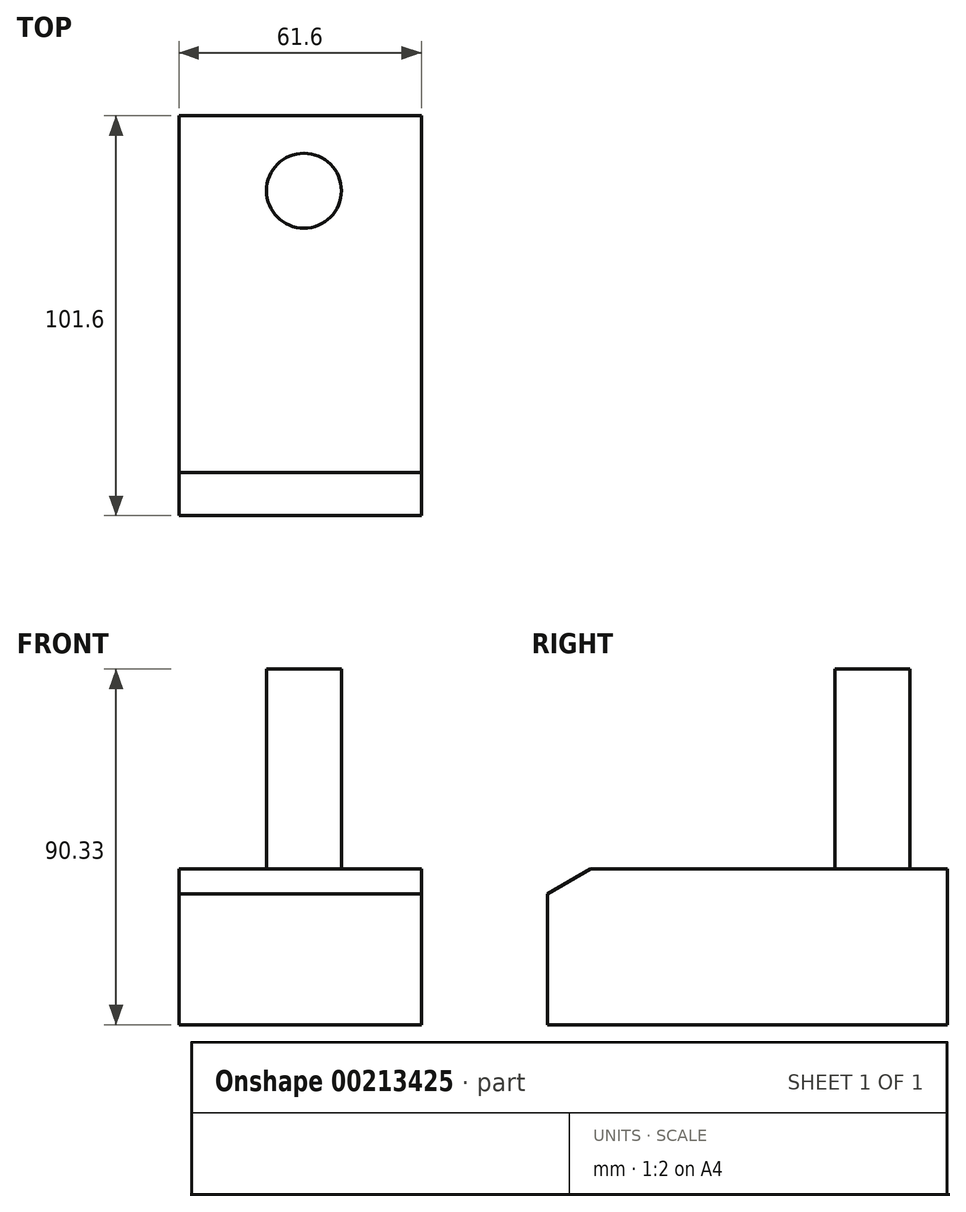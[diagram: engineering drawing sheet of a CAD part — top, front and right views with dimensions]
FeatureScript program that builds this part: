
annotation { "Feature Type Name" : "Feature", "Feature Type Description" : "" }
export const myFeature = defineFeature(function(context is Context, id is Id, definition is map)
    precondition{}
    {
        {
            var Q0;
            Q0=qCreatedBy(makeId("Front.planeOp"),FACE);
            var sketch = newSketch(context, id + "F0", { "sketchPlane" : qUnion([Q0])});
            skLineSegment(sketch, "E0", {"start": v(0, 0) * mm, "end": v(61.6, 0) * mm});
            skLineSegment(sketch, "E1", {"start": v(61.6, 0) * mm, "end": v(61.6, 39.53) * mm});
            skLineSegment(sketch, "E2", {"start": v(61.6, 39.53) * mm, "end": v(0, 39.53) * mm});
            skLineSegment(sketch, "E3", {"start": v(0, 39.53) * mm, "end": v(0, 0) * mm});
            skSolve(sketch);
        }
        {
            var Q0;
            Q0 = qSketchRegion(id + "F0", true);
            extrude(context, id + "F1", {"entities" : qUnion([Q0]), "depth" : 101.6 * mm});
        }
        {
            var Q0;
            Q0=makeQuery(id+"F1.opExtrude","CAP_EDGE",EDGE,{"disambiguationData":[OSD([sQuery(id+"F0.wireOp",EDGE,"E2")])],"isStart":false});
            chamfer(context, id + "F2", {"entities" : qUnion([Q0]), "chamferType" : ChamferType.OFFSET_ANGLE, "width" : 6.35 * mm, "oppositeDirection" : false, "angle" : 60 * degree, "tangentPropagation" : true});
        }
        {
            var Q0;
            Q0=makeQuery(id+"F1.opExtrude","SWEPT_FACE",FACE,{"disambiguationData":[OSD([sQuery(id+"F0.wireOp",EDGE,"E2")])]});
            var sketch = newSketch(context, id + "F3", { "sketchPlane" : qUnion([Q0])});
            skCircle(sketch, "E4", {"center": v(31.75, -19.05) * mm, "radius": 9.53 * mm});
            skSolve(sketch);
        }
        {
            var Q0;
            Q0=makeQuery(id+"F3.imprint","IMPRINT",FACE,{"disambiguationData":[TD([[makeQuery(id+"F3.imprint","IMPRINT",EDGE,{"derivedFrom":sQuery(id+"F3.wireOp",EDGE,"E4")}),1.0]])]});
            var Q1;
            Q1=sQuery(id+"F3.wireOp",EDGE,"E4");
            extrude(context, id + "F4", {"entities" : qUnion([Q0]), "surfaceEntities" : qUnion([Q1]), "depth" : 50.8 * mm});
        }
    });
